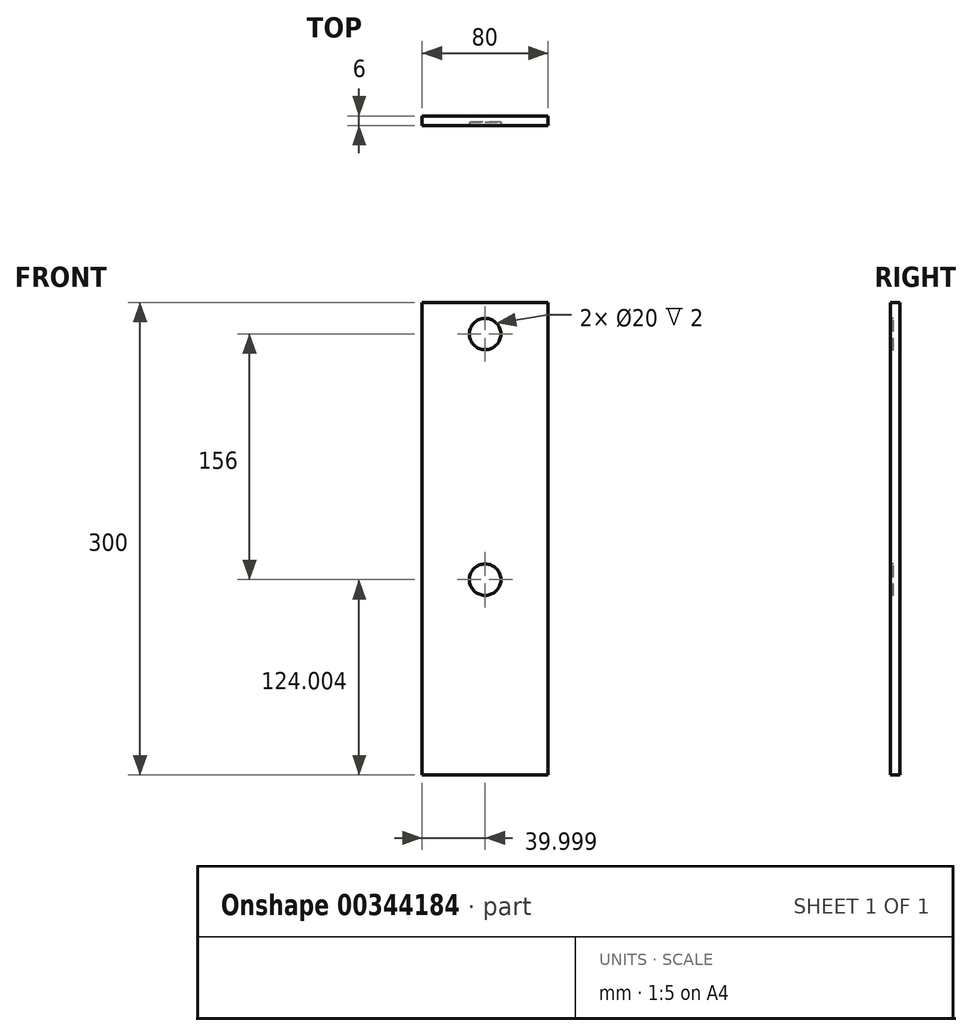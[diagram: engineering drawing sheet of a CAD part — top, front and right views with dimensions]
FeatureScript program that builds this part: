
annotation { "Feature Type Name" : "Feature", "Feature Type Description" : "" }
export const myFeature = defineFeature(function(context is Context, id is Id, definition is map)
    precondition{}
    {
        {
            var Q0;
            Q0=qCreatedBy(makeId("Front.planeOp"),FACE);
            var sketch = newSketch(context, id + "F0", { "sketchPlane" : qUnion([Q0])});
            skLineSegment(sketch, "E0.bottom", {"start": v(-48.2, 197.8) * mm, "end": v(31.8, 197.8) * mm});
            skLineSegment(sketch, "E0.top", {"start": v(-48.2, -102.2) * mm, "end": v(31.8, -102.2) * mm});
            skLineSegment(sketch, "E0.left", {"start": v(-48.2, 197.8) * mm, "end": v(-48.2, -102.2) * mm});
            skLineSegment(sketch, "E0.right", {"start": v(31.8, 197.8) * mm, "end": v(31.8, -102.2) * mm});
            skSolve(sketch);
        }
        {
            var Q0;
            Q0 = qSketchRegion(id + "F0", true);
            extrude(context, id + "F1", {"entities" : qUnion([Q0]), "depth" : 6 * mm});
        }
        {
            var Q0;
            Q0=makeQuery(id+"F1.opExtrude","CAP_FACE",FACE,{"disambiguationData":[OSD([sQuery(id+"F0.wireOp",EDGE,"E0.bottom"),sQuery(id+"F0.wireOp",EDGE,"E0.top"),sQuery(id+"F0.wireOp",EDGE,"E0.left"),sQuery(id+"F0.wireOp",EDGE,"E0.right")])],"isStart":false});
            var sketch = newSketch(context, id + "F2", { "sketchPlane" : qUnion([Q0])});
            skLineSegment(sketch, "E1", {"start": v(-8.2, 177.8) * mm, "end": v(-8.2, 21.8) * mm, "construction": true});
            skLineSegment(sketch, "E2", {"start": v(-8.2, 21.8) * mm, "end": v(7.32, 21.8) * mm, "construction": true});
            skLineSegment(sketch, "E3", {"start": v(-8.2, 177.8) * mm, "end": v(-5, 177.8) * mm, "construction": true});
            skCircle(sketch, "E4", {"center": v(-8.2, 177.8) * mm, "radius": 10 * mm});
            skCircle(sketch, "E5", {"center": v(-8.2, 21.8) * mm, "radius": 10 * mm});
            skSolve(sketch);
        }
        {
            var Q0;
            Q0 = qSketchRegion(id + "F2", true);
            extrude(context, id + "F3", {"entities" : qUnion([Q0]), "operationType" : NewBodyOperationType.REMOVE, "oppositeDirection" : true, "depth" : 2 * mm});
        }
    });
